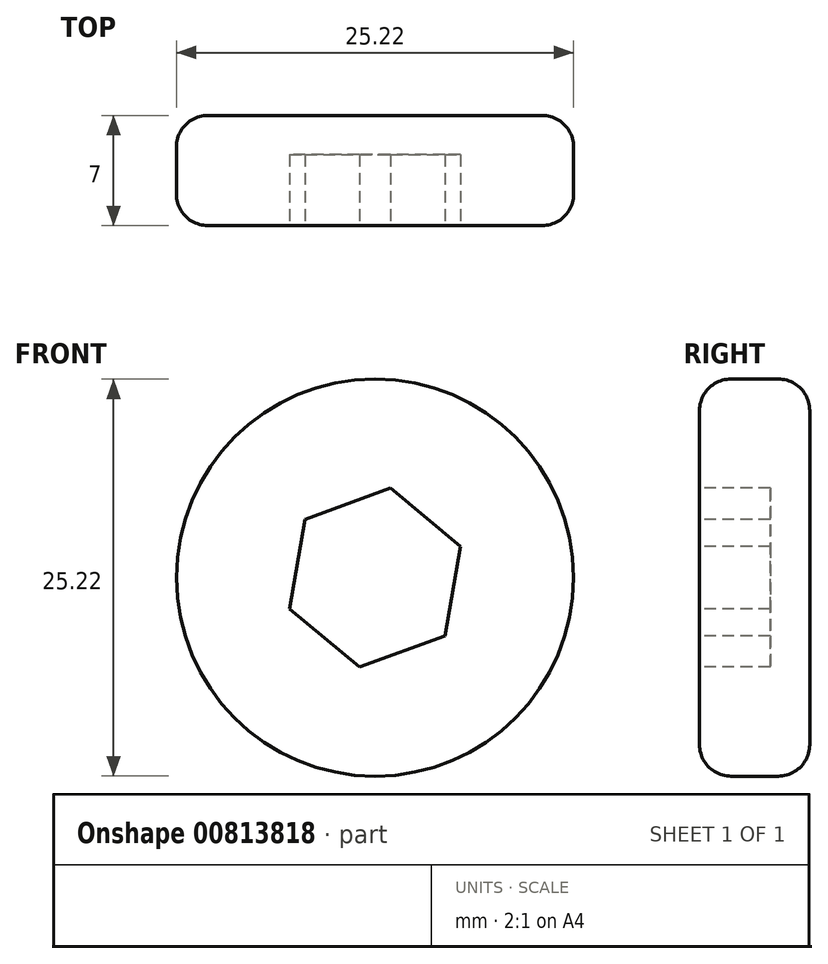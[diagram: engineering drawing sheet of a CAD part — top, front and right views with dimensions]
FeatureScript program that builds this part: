
annotation { "Feature Type Name" : "Feature", "Feature Type Description" : "" }
export const myFeature = defineFeature(function(context is Context, id is Id, definition is map)
    precondition{}
    {
        {
            var Q0;
            Q0=qCreatedBy(makeId("Front.planeOp"),FACE);
            var sketch = newSketch(context, id + "F0", { "sketchPlane" : qUnion([Q0])});
            skCircle(sketch, "E0", {"center": v(0, 0) * mm, "radius": 12.61 * mm});
            skSolve(sketch);
        }
        {
            var Q0;
            Q0 = qSketchRegion(id + "F0", true);
            extrude(context, id + "F1", {"entities" : qUnion([Q0]), "depth" : 7 * mm, "offsetDistance" : 25 * mm});
        }
        {
            var Q0;
            Q0=makeQuery(id+"F1.opExtrude","CAP_FACE",FACE,{"disambiguationData":[OSD([sQuery(id+"F0.wireOp",EDGE,"E0")])],"isStart":false});
            var sketch = newSketch(context, id + "F2", { "sketchPlane" : qUnion([Q0])});
            skCircle(sketch, "E1.cCircle", {"center": v(0, 0) * mm, "radius": 5 * mm, "construction": true});
            skLineSegment(sketch, "E1.0", {"start": v(5.42, 2) * mm, "end": v(4.43, -3.7) * mm});
            skLineSegment(sketch, "E1.1", {"start": v(4.43, -3.7) * mm, "end": v(-0.99, -5.69) * mm});
            skLineSegment(sketch, "E1.2", {"start": v(-0.99, -5.69) * mm, "end": v(-5.42, -2) * mm});
            skLineSegment(sketch, "E1.3", {"start": v(-5.42, -2) * mm, "end": v(-4.43, 3.7) * mm});
            skLineSegment(sketch, "E1.4", {"start": v(-4.43, 3.7) * mm, "end": v(0.99, 5.69) * mm});
            skLineSegment(sketch, "E1.5", {"start": v(0.99, 5.69) * mm, "end": v(5.42, 2) * mm});
            skPoint(sketch, "E1.0.midPoint", {"position": v(4.93, -0.85) * mm});
            skSolve(sketch);
        }
        {
            var Q0;
            Q0 = qSketchRegion(id + "F2", true);
            extrude(context, id + "F3", {"entities" : qUnion([Q0]), "operationType" : NewBodyOperationType.REMOVE, "oppositeDirection" : true, "depth" : 4.5 * mm, "offsetDistance" : 25 * mm});
        }
        {
            var Q0;
            Q0=makeQuery(id+"F1.opExtrude","CAP_EDGE",EDGE,{"disambiguationData":[OSD([sQuery(id+"F0.wireOp",EDGE,"E0")])],"isStart":false});
            var Q1;
            Q1=makeQuery(id+"F1.opExtrude","CAP_EDGE",EDGE,{"disambiguationData":[OSD([sQuery(id+"F0.wireOp",EDGE,"E0")])],"isStart":true});
            fillet(context, id + "F4", {"entities" : qUnion([Q0, Q1]), "radius" : 2 * mm, "tangentPropagation" : true, "allowEdgeOverflow" : false});
        }
    });
